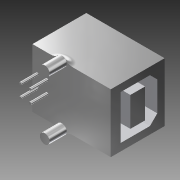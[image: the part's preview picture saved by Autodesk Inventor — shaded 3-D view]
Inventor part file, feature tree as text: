
AUTODESK INVENTOR PART (.ipt)
format: ipt  version: 2014 (Build 180170000, 170)  size: 199,168 bytes
history: native  units: mm
features: extrude x3, sketch x3, fillet x1
ambient origin geometry x8: Origin, YZ Plane, XZ Plane, XY Plane, X Axis, Y Axis, Z Axis, Center Point
bodies: Solid1 (feature_tree)
feature tree (7):
  extrude  "Extrusion1"  Depth=12.0mm
  extrude  "Extrusion2"  Depth=8.0mm
  extrude  "Extrusion3"  Depth=1.5mm
  fillet  "Fillet1"  Radius=1.5mm
  sketch  "Sketch1"  dims[d0=16.0mm d1=12.0mm]
  sketch  "Sketch2"  dims[d2=6.0mm d3=8.0mm]
  sketch  "Sketch3"  dims[d4=11.0mm d5=0.0mm d6=1.5mm d7=1.5mm d8=1.5mm d9=2.0mm d10=45.0deg d11=45.0deg d12=3.0mm d13=3.0mm d14=3.0mm d15=4.0mm d16=6.0mm d17=3.0mm d18=3.0mm d19=9.0mm d20=0.0mm d21=0.5mm d22=0.5mm d23=0.5mm d25=0.5mm d26=2.5mm d27=2.5mm d28=1.25mm d29=0.0mm d30=1.0mm d31=2.0mm d32=2.0mm d34=1.0mm d35=2.0mm d36=6.0mm d37=6.0mm d38=0.0mm d39=0.0mm d40=3.5mm d41=0.0mm d42=2.0mm]
